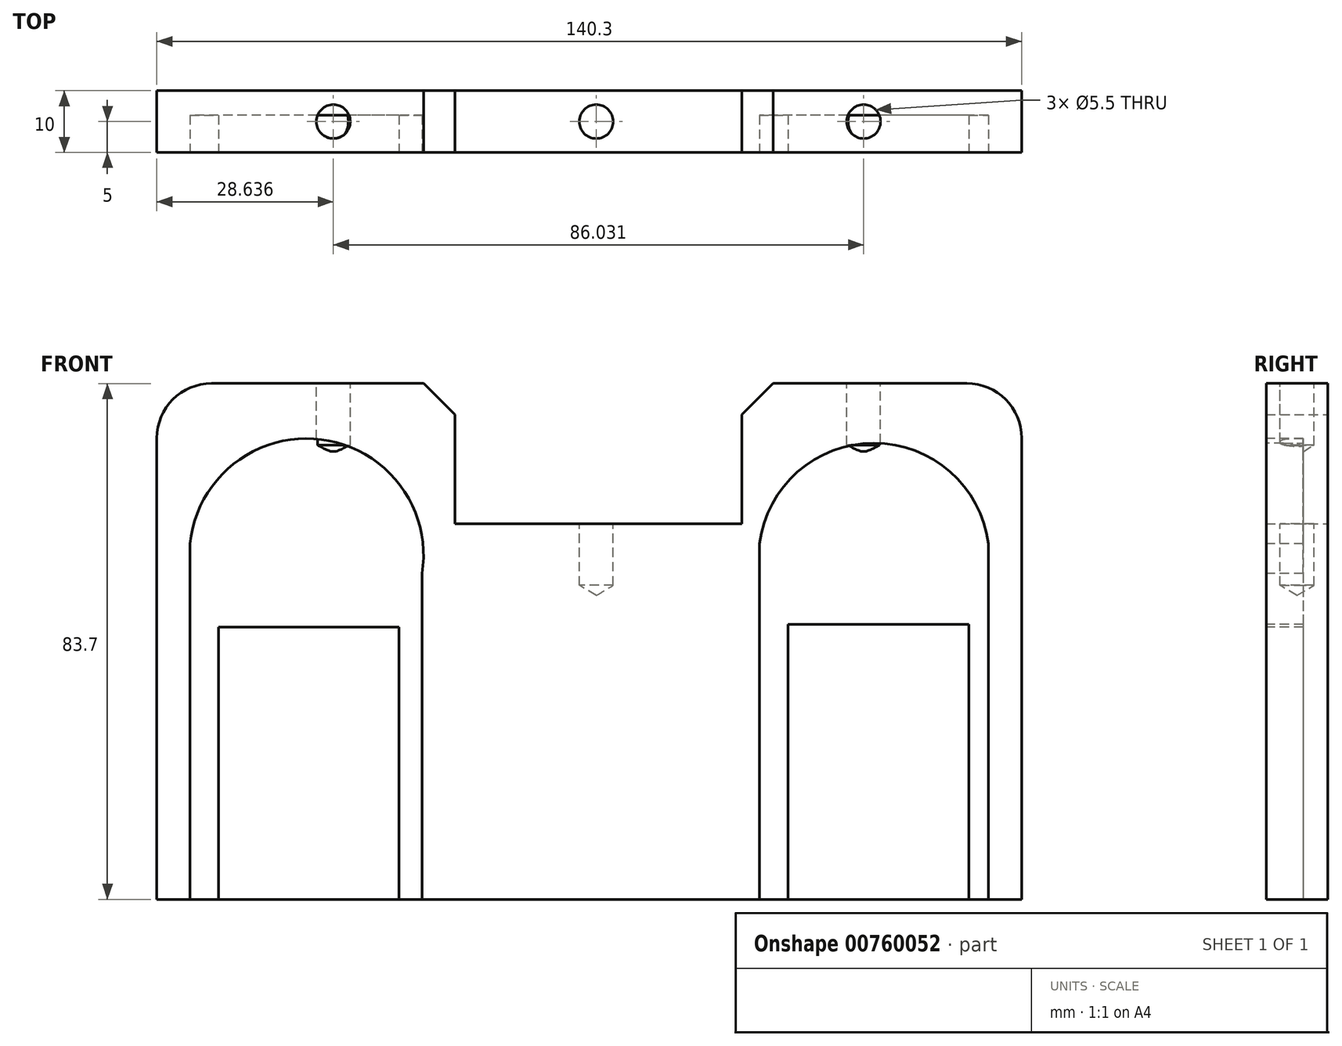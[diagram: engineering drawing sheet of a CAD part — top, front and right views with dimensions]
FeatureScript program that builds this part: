
annotation { "Feature Type Name" : "Feature", "Feature Type Description" : "" }
export const myFeature = defineFeature(function(context is Context, id is Id, definition is map)
    precondition{}
    {
        {
            var Q0;
            Q0=qCreatedBy(makeId("Front.planeOp"),FACE);
            var sketch = newSketch(context, id + "F0", { "sketchPlane" : qUnion([Q0])});
            skLineSegment(sketch, "E0.bottom", {"start": v(-71.29, 28.26) * mm, "end": v(69.01, 28.26) * mm});
            skLineSegment(sketch, "E0.top", {"start": v(-71.29, -32.68) * mm, "end": v(69.01, -32.68) * mm});
            skLineSegment(sketch, "E0.left", {"start": v(-71.29, 28.26) * mm, "end": v(-71.29, -32.68) * mm});
            skLineSegment(sketch, "E0.right", {"start": v(69.01, 28.26) * mm, "end": v(69.01, -32.68) * mm});
            skLineSegment(sketch, "E1.bottom", {"start": v(-71.29, 28.26) * mm, "end": v(-22.9, 28.26) * mm});
            skLineSegment(sketch, "E1.top", {"start": v(-62.4, 51.02) * mm, "end": v(-22.9, 51.02) * mm});
            skLineSegment(sketch, "E1.left", {"start": v(-71.29, 28.26) * mm, "end": v(-71.29, 42.13) * mm});
            skLineSegment(sketch, "E1.right", {"start": v(-22.9, 28.26) * mm, "end": v(-22.9, 51.02) * mm});
            skLineSegment(sketch, "E2.bottom", {"start": v(69.01, 28.26) * mm, "end": v(23.6, 28.26) * mm});
            skLineSegment(sketch, "E2.top", {"start": v(60.12, 51.02) * mm, "end": v(23.6, 51.02) * mm});
            skLineSegment(sketch, "E2.left", {"start": v(69.01, 28.26) * mm, "end": v(69.01, 42.13) * mm});
            skLineSegment(sketch, "E2.right", {"start": v(23.6, 28.26) * mm, "end": v(23.6, 51.02) * mm});
            skPoint(sketch, "E3.visualSharp", {"position": v(-71.29, 51.02) * mm});
            skArc(sketch, "E3.filletArc", {"start": v(-62.4, 51.02) * mm, "mid": v(-68.68, 48.42) * mm, "end": v(-71.29, 42.13) * mm});
            skPoint(sketch, "E4.visualSharp", {"position": v(69.01, 51.02) * mm});
            skArc(sketch, "E4.filletArc", {"start": v(69.01, 42.13) * mm, "mid": v(66.4, 48.42) * mm, "end": v(60.12, 51.02) * mm});
            skSolve(sketch);
        }
        {
            var Q0;
            Q0 = qSketchRegion(id + "F0", true);
            extrude(context, id + "F1", {"entities" : qUnion([Q0]), "endBound" : BoundingType.SYMMETRIC, "depth" : 10 * mm, "offsetDistance" : 25.4 * mm});
        }
        {
            var Q0;
            Q0=makeQuery(id+"F1.opExtrude","SWEPT_FACE",FACE,{"disambiguationData":[OSD([sQuery(id+"F0.wireOp",EDGE,"E1.top")])]});
            var sketch = newSketch(context, id + "F2", { "sketchPlane" : qUnion([Q0])});
            skCircle(sketch, "E5", {"center": v(-42.65, 0) * mm, "radius": 3.63 * mm});
            skPoint(sketch, "E5.centerSnap0", {"position": v(-42.65, -5) * mm});
            skSolve(sketch);
        }
        {
            var Q0;
            Q0=makeQuery(id+"F1.opExtrude","SWEPT_FACE",FACE,{"disambiguationData":[OSD([sQuery(id+"F0.wireOp",EDGE,"E2.top")])]});
            var sketch = newSketch(context, id + "F3", { "sketchPlane" : qUnion([Q0])});
            skCircle(sketch, "E6", {"center": v(43.38, 0) * mm, "radius": 3.64 * mm});
            skSolve(sketch);
        }
        {
            var Q0;
            Q0=sQuery(id+"F2.wireOp",VERTEX,"E5.center");
            var Q1;
            Q1=makeQuery(id+"F1.opExtrude","SWEPT_BODY",BODY,{"disambiguationData":[OSD([sQuery(id+"F0.wireOp",EDGE,"E0.bottom"),sQuery(id+"F0.wireOp",EDGE,"E0.top"),sQuery(id+"F0.wireOp",EDGE,"E0.left"),sQuery(id+"F0.wireOp",EDGE,"E0.right"),sQuery(id+"F0.wireOp",EDGE,"E1.top"),sQuery(id+"F0.wireOp",EDGE,"E1.left"),sQuery(id+"F0.wireOp",EDGE,"E1.right"),sQuery(id+"F0.wireOp",EDGE,"E2.top"),sQuery(id+"F0.wireOp",EDGE,"E2.left"),sQuery(id+"F0.wireOp",EDGE,"E2.right"),sQuery(id+"F0.wireOp",EDGE,"E3.filletArc"),sQuery(id+"F0.wireOp",EDGE,"E4.filletArc")])]});
            hole(context, id + "F4", {"style" : HoleStyle.SIMPLE, "endStyle" : HoleEndStyle.BLIND, "standardTappedOrClearance" : lookupTablePath({ "standard" : "ISO", "fit" : "Normal", "size" : "M5", "type" : "Clearance" }), "standardBlindInLast" : lookupTablePath({ "fit" : "Standard", "standard" : "ISO", "size" : "M5", "type" : "Clearance" }), "holeDiameter" : 5.5 * mm, "majorDiameter" : 6.35 * mm, "holeDepth" : 10 * mm, "isTappedThrough" : true, "tappedDepth" : 12.7 * mm, "tapClearance" : 3, "startFromSketch" : true, "locations" : qUnion([Q0]), "scope" : qUnion([Q1])});
        }
        {
            var Q0;
            Q0=sQuery(id+"F3.wireOp",VERTEX,"E6.center");
            var Q1;
            Q1=makeQuery(id+"F1.opExtrude","SWEPT_BODY",BODY,{"disambiguationData":[OSD([sQuery(id+"F0.wireOp",EDGE,"E0.bottom"),sQuery(id+"F0.wireOp",EDGE,"E0.top"),sQuery(id+"F0.wireOp",EDGE,"E0.left"),sQuery(id+"F0.wireOp",EDGE,"E0.right"),sQuery(id+"F0.wireOp",EDGE,"E1.top"),sQuery(id+"F0.wireOp",EDGE,"E1.left"),sQuery(id+"F0.wireOp",EDGE,"E1.right"),sQuery(id+"F0.wireOp",EDGE,"E2.top"),sQuery(id+"F0.wireOp",EDGE,"E2.left"),sQuery(id+"F0.wireOp",EDGE,"E2.right"),sQuery(id+"F0.wireOp",EDGE,"E3.filletArc"),sQuery(id+"F0.wireOp",EDGE,"E4.filletArc")])]});
            hole(context, id + "F5", {"style" : HoleStyle.SIMPLE, "endStyle" : HoleEndStyle.BLIND, "standardTappedOrClearance" : lookupTablePath({ "standard" : "ISO", "fit" : "Normal", "size" : "M5", "type" : "Clearance" }), "standardBlindInLast" : lookupTablePath({ "fit" : "Standard", "standard" : "ISO", "size" : "M5", "type" : "Clearance" }), "holeDiameter" : 5.5 * mm, "majorDiameter" : 6.35 * mm, "holeDepth" : 10 * mm, "isTappedThrough" : true, "tappedDepth" : 12.7 * mm, "tapClearance" : 3, "startFromSketch" : true, "locations" : qUnion([Q0]), "scope" : qUnion([Q1])});
        }
        {
            var Q0;
            Q0=makeQuery(id+"F1.opExtrude","SWEPT_FACE",FACE,{"disambiguationData":[OSD([sQuery(id+"F0.wireOp",EDGE,"E0.bottom")])]});
            var sketch = newSketch(context, id + "F6", { "sketchPlane" : qUnion([Q0])});
            skCircle(sketch, "E7", {"center": v(0, 0) * mm, "radius": 3.64 * mm});
            skSolve(sketch);
        }
        {
            var Q0;
            Q0=sQuery(id+"F6.wireOp",VERTEX,"E7.center");
            var Q1;
            Q1=makeQuery(id+"F1.opExtrude","SWEPT_BODY",BODY,{"disambiguationData":[OSD([sQuery(id+"F0.wireOp",EDGE,"E0.bottom"),sQuery(id+"F0.wireOp",EDGE,"E0.top"),sQuery(id+"F0.wireOp",EDGE,"E0.left"),sQuery(id+"F0.wireOp",EDGE,"E0.right"),sQuery(id+"F0.wireOp",EDGE,"E1.top"),sQuery(id+"F0.wireOp",EDGE,"E1.left"),sQuery(id+"F0.wireOp",EDGE,"E1.right"),sQuery(id+"F0.wireOp",EDGE,"E2.top"),sQuery(id+"F0.wireOp",EDGE,"E2.left"),sQuery(id+"F0.wireOp",EDGE,"E2.right"),sQuery(id+"F0.wireOp",EDGE,"E3.filletArc"),sQuery(id+"F0.wireOp",EDGE,"E4.filletArc")])]});
            hole(context, id + "F7", {"style" : HoleStyle.SIMPLE, "endStyle" : HoleEndStyle.BLIND, "standardTappedOrClearance" : lookupTablePath({ "standard" : "ISO", "fit" : "Normal", "size" : "M5", "type" : "Clearance" }), "standardBlindInLast" : lookupTablePath({ "fit" : "Standard", "standard" : "ISO", "size" : "M5", "type" : "Clearance" }), "holeDiameter" : 5.5 * mm, "majorDiameter" : 6.35 * mm, "holeDepth" : 10 * mm, "isTappedThrough" : true, "tappedDepth" : 12.7 * mm, "tapClearance" : 3, "startFromSketch" : true, "locations" : qUnion([Q0]), "scope" : qUnion([Q1])});
        }
        {
            var Q0;
            Q0=makeQuery(id+"F1.opExtrude","CAP_FACE",FACE,{"disambiguationData":[OSD([sQuery(id+"F0.wireOp",EDGE,"E0.bottom"),sQuery(id+"F0.wireOp",EDGE,"E0.top"),sQuery(id+"F0.wireOp",EDGE,"E0.left"),sQuery(id+"F0.wireOp",EDGE,"E0.right"),sQuery(id+"F0.wireOp",EDGE,"E1.top"),sQuery(id+"F0.wireOp",EDGE,"E1.left"),sQuery(id+"F0.wireOp",EDGE,"E1.right"),sQuery(id+"F0.wireOp",EDGE,"E2.top"),sQuery(id+"F0.wireOp",EDGE,"E2.left"),sQuery(id+"F0.wireOp",EDGE,"E2.right"),sQuery(id+"F0.wireOp",EDGE,"E3.filletArc"),sQuery(id+"F0.wireOp",EDGE,"E4.filletArc")])],"isStart":false});
            var sketch = newSketch(context, id + "F8", { "sketchPlane" : qUnion([Q0])});
            skArc(sketch, "E8", {"start": v(-28.26, 20.17) * mm, "mid": v(-46.5, 42.08) * mm, "end": v(-65.9, 21.2) * mm});
            skLineSegment(sketch, "E9.bottom", {"start": v(-65.9, 25) * mm, "end": v(-28.26, 25) * mm});
            skLineSegment(sketch, "E9.top", {"start": v(-65.9, -32.68) * mm, "end": v(-28.26, -32.68) * mm});
            skLineSegment(sketch, "E9.left", {"start": v(-65.9, 25) * mm, "end": v(-65.9, -32.68) * mm});
            skLineSegment(sketch, "E9.right", {"start": v(-28.26, 25) * mm, "end": v(-28.26, -32.68) * mm});
            skLineSegment(sketch, "E10.left", {"start": v(-31.98, 11.51) * mm, "end": v(-31.98, 11.51) * mm});
            skLineSegment(sketch, "E10.right", {"start": v(-28.26, 11.51) * mm, "end": v(-28.26, 11.51) * mm});
            skLineSegment(sketch, "E11.bottom", {"start": v(-31.98, 11.51) * mm, "end": v(-61.29, 11.51) * mm});
            skLineSegment(sketch, "E11.top", {"start": v(-31.98, -32.68) * mm, "end": v(-61.29, -32.68) * mm});
            skLineSegment(sketch, "E11.left", {"start": v(-31.98, 11.51) * mm, "end": v(-31.98, -32.68) * mm});
            skLineSegment(sketch, "E11.right", {"start": v(-61.29, 11.51) * mm, "end": v(-61.29, -32.68) * mm});
            skPoint(sketch, "E12.orphan", {"position": v(-61.29, 10.58) * mm});
            skSolve(sketch);
        }
        {
            var Q0;
            {var subQ3=sQuery(id+"F8.wireOp",EDGE,"E9.bottom");Q0=makeQuery(id+"F8.imprint","IMPRINT",FACE,{"disambiguationData":[TD([[makeQuery(id+"F8.imprint","IMPRINT",EDGE,{"derivedFrom":subQ3}),1.0]])]});}
            var Q1;
            {var subQ3=sQuery(id+"F8.wireOp",EDGE,"E9.bottom");Q1=makeQuery(id+"F8.imprint","IMPRINT",FACE,{"disambiguationData":[TD([[makeQuery(id+"F8.imprint","IMPRINT",EDGE,{"derivedFrom":subQ3}),-1.0]])]});}
            extrude(context, id + "F9", {"entities" : qUnion([Q0, Q1]), "operationType" : NewBodyOperationType.REMOVE, "oppositeDirection" : true, "depth" : 6 * mm, "offsetDistance" : 25.4 * mm});
        }
        {
            var Q0;
            {var subQ0=sQuery(id+"F0.wireOp",EDGE,"E3.filletArc");var subQ1=sQuery(id+"F0.wireOp",EDGE,"E2.right");var subQ2=sQuery(id+"F0.wireOp",EDGE,"E2.top");var subQ3=sQuery(id+"F0.wireOp",EDGE,"E1.right");var subQ4=sQuery(id+"F0.wireOp",EDGE,"E1.top");var subQ5=sQuery(id+"F0.wireOp",EDGE,"E4.filletArc");var subQ6=sQuery(id+"F0.wireOp",EDGE,"E0.bottom");var subQ7=sQuery(id+"F0.wireOp",EDGE,"E2.left");var subQ8=sQuery(id+"F0.wireOp",EDGE,"E0.right");var subQ9=sQuery(id+"F0.wireOp",EDGE,"E0.top");var subQ10=sQuery(id+"F0.wireOp",EDGE,"E1.left");var subQ11=sQuery(id+"F0.wireOp",EDGE,"E0.left");Q0=makeQuery(id+"F9.boolean.opBoolean","SPLIT",FACE,{"disambiguationData":[TD([makeQuery(id+"F1.opExtrude","SWEPT_FACE",FACE,{"disambiguationData":[OSD([subQ6])]})])],"derivedFrom":makeQuery(id+"F1.opExtrude","CAP_FACE",FACE,{"disambiguationData":[OSD([subQ6,subQ9,subQ11,subQ8,subQ4,subQ10,subQ3,subQ2,subQ7,subQ1,subQ0,subQ5])],"isStart":false})});}
            var sketch = newSketch(context, id + "F10", { "sketchPlane" : qUnion([Q0])});
            skArc(sketch, "E13", {"start": v(63.63, 25) * mm, "mid": v(42.68, 41.22) * mm, "end": v(26.47, 20.26) * mm});
            skLineSegment(sketch, "E14.bottom", {"start": v(26.47, 25) * mm, "end": v(63.63, 25) * mm});
            skLineSegment(sketch, "E14.top", {"start": v(26.47, -32.68) * mm, "end": v(63.63, -32.68) * mm});
            skLineSegment(sketch, "E14.left", {"start": v(26.47, 25) * mm, "end": v(26.47, -32.68) * mm});
            skLineSegment(sketch, "E14.right", {"start": v(63.63, 25) * mm, "end": v(63.63, -32.68) * mm});
            skLineSegment(sketch, "E15.left", {"start": v(60.43, 11.94) * mm, "end": v(60.43, 11.94) * mm});
            skLineSegment(sketch, "E15.right", {"start": v(63.63, 11.94) * mm, "end": v(63.63, 11.94) * mm});
            skLineSegment(sketch, "E16.bottom", {"start": v(60.43, 11.94) * mm, "end": v(31.12, 11.94) * mm});
            skLineSegment(sketch, "E16.top", {"start": v(60.43, -32.68) * mm, "end": v(31.12, -32.68) * mm});
            skLineSegment(sketch, "E16.left", {"start": v(60.43, 11.94) * mm, "end": v(60.43, -32.68) * mm});
            skLineSegment(sketch, "E16.right", {"start": v(31.12, 11.94) * mm, "end": v(31.12, -32.68) * mm});
            skPoint(sketch, "E17.orphan", {"position": v(31.12, 10.1) * mm});
            skSolve(sketch);
        }
        {
            var Q0;
            {var subQ0=sQuery(id+"F10.wireOp",EDGE,"E14.bottom");Q0=makeQuery(id+"F10.imprint","IMPRINT",FACE,{"disambiguationData":[TD([[makeQuery(id+"F10.imprint","IMPRINT",EDGE,{"derivedFrom":subQ0}),1.0]])]});}
            var Q1;
            {var subQ3=sQuery(id+"F10.wireOp",EDGE,"E14.bottom");Q1=makeQuery(id+"F10.imprint","IMPRINT",FACE,{"disambiguationData":[TD([[makeQuery(id+"F10.imprint","IMPRINT",EDGE,{"derivedFrom":subQ3}),-1.0]])]});}
            extrude(context, id + "F11", {"entities" : qUnion([Q0, Q1]), "operationType" : NewBodyOperationType.REMOVE, "oppositeDirection" : true, "depth" : 6 * mm, "offsetDistance" : 25.4 * mm});
        }
        {
            var Q0;
            Q0=makeQuery(id+"F1.opExtrude","SWEPT_EDGE",EDGE,{"disambiguationData":[OSD([sQuery(id+"F0.wireOp",EDGE,"E1.top"),sQuery(id+"F0.wireOp",EDGE,"E1.right")])]});
            chamfer(context, id + "F12", {"entities" : qUnion([Q0]), "width" : 5.08 * mm, "tangentPropagation" : true});
        }
        {
            var Q0;
            Q0=makeQuery(id+"F1.opExtrude","SWEPT_EDGE",EDGE,{"disambiguationData":[OSD([sQuery(id+"F0.wireOp",EDGE,"E2.top"),sQuery(id+"F0.wireOp",EDGE,"E2.right")])]});
            chamfer(context, id + "F13", {"entities" : qUnion([Q0]), "width" : 5.08 * mm, "tangentPropagation" : true});
        }
    });
